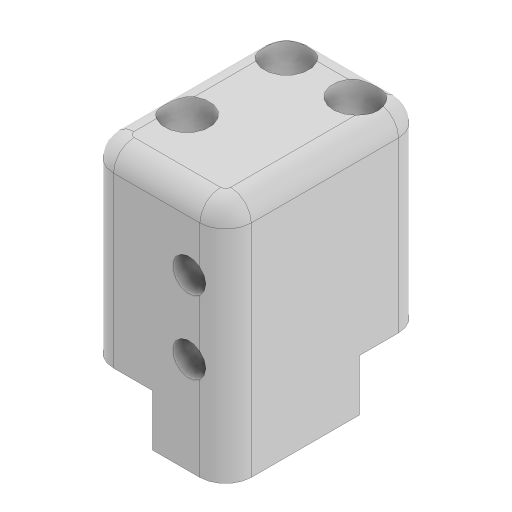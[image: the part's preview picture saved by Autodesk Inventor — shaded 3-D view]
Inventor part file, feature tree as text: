
AUTODESK INVENTOR PART (.ipt)
format: ipt  version: 2024 (Build 280153000, 153)  size: 323,072 bytes
history: native  units: in
note: dims shown in document units (in); Inventor stores cm internally (conversion verified against a paired STEP export)
features: sketch x6, extrude x4, fillet x2, plane x1, mirror x1, projected_geometry x1
ambient origin geometry x8: Origin, YZ Plane, XZ Plane, XY Plane, X Axis, Y Axis, Z Axis, Center Point
bodies: Solid1 (feature_tree)
feature tree (15):
  extrude  "Extrusion1"  Depth=0.92in TaperAngle=0.0deg
  extrude  "Extrusion2"  Depth=0.1in
  fillet  "Fillet1"  Radius=0.2165in
  fillet  "Fillet2"  Radius=0.2165in
  extrude  "Extrusion3"  Depth=0.625in TaperAngle=0.0deg
  sketch  "Sketch4"  dims[d11=0.0in d12=0.0in]
  sketch  "Sketch5"
  plane  "Work Plane1"
  mirror  "Mirror1"
  extrude  "Extrusion4"  [1 undecoded]
  sketch  "Sketch1"  dims[d0=0.65in d1=0.0in d2=0.92in d3=0.0in]
  sketch  "Sketch2"  dims[d4=0.125in d5=0.1in d6=0.2165in d7=0.2165in]
  projected_geometry  "Projected Loop1"
  sketch  "Sketch3"  dims[d8=0.2165in d9=0.625in d10=0.0in]
  sketch  "Sketch6"
note: 1 required parameter value undecoded (feature->parameter linkage not recoverable at this tier; creation-order binding heuristic only, values carry confidence <= 0.55)
